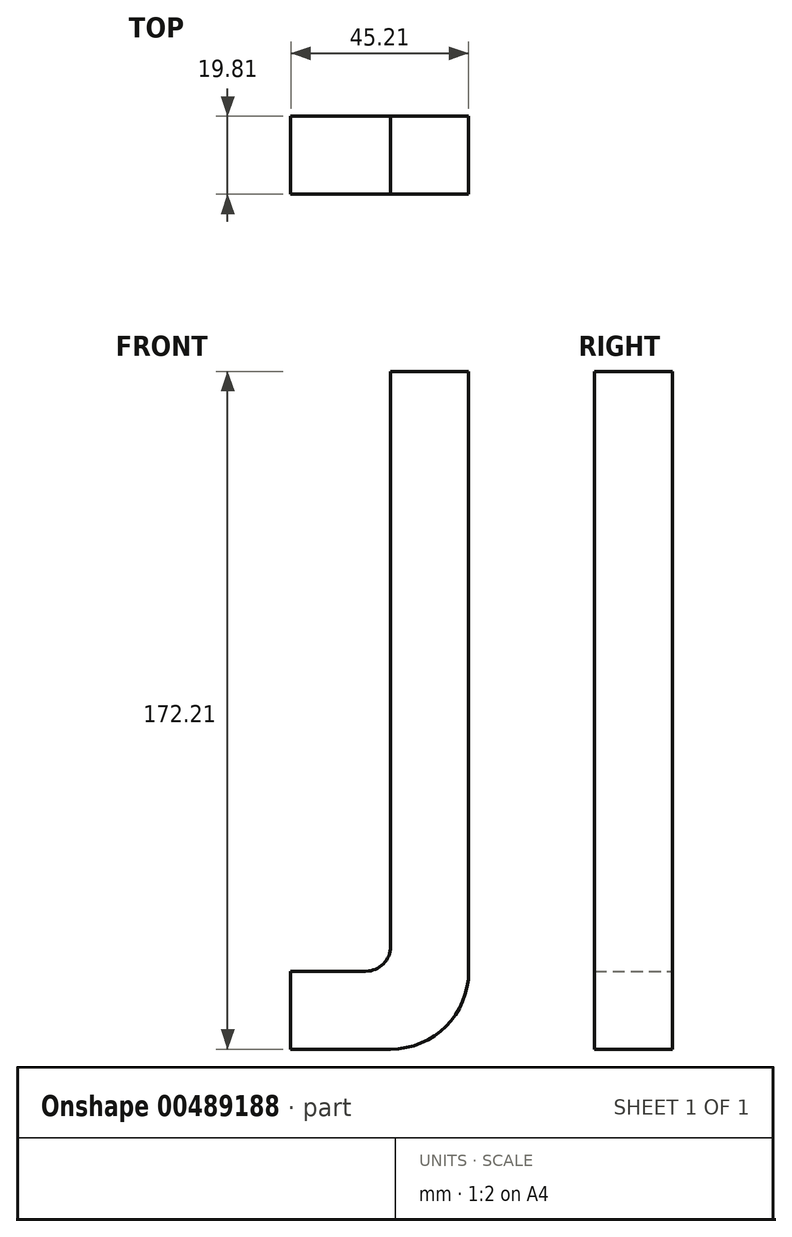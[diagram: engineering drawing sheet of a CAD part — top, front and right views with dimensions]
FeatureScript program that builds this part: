
annotation { "Feature Type Name" : "Feature", "Feature Type Description" : "" }
export const myFeature = defineFeature(function(context is Context, id is Id, definition is map)
    precondition{}
    {
        {
            var Q0;
            Q0=qCreatedBy(makeId("Front.planeOp"),FACE);
            var sketch = newSketch(context, id + "F0", { "sketchPlane" : qUnion([Q0])});
            skLineSegment(sketch, "E0.bottom", {"start": v(-36.32, 115.57) * mm, "end": v(-16.51, 115.57) * mm});
            skLineSegment(sketch, "E0.left", {"start": v(-36.32, 115.57) * mm, "end": v(-36.32, -30.48) * mm});
            skLineSegment(sketch, "E0.right", {"start": v(-16.51, 115.57) * mm, "end": v(-16.51, -36.83) * mm});
            skArc(sketch, "E1", {"start": v(-36.32, -56.64) * mm, "mid": v(-22.32, -50.84) * mm, "end": v(-16.51, -36.83) * mm});
            skLineSegment(sketch, "E2.bottom", {"start": v(-36.32, -56.64) * mm, "end": v(-61.72, -56.64) * mm});
            skLineSegment(sketch, "E2.top", {"start": v(-42.67, -36.83) * mm, "end": v(-61.72, -36.83) * mm});
            skLineSegment(sketch, "E2.right", {"start": v(-61.72, -56.64) * mm, "end": v(-61.72, -36.83) * mm});
            skArc(sketch, "E3.filletArc", {"start": v(-42.67, -36.83) * mm, "mid": v(-38.18, -34.97) * mm, "end": v(-36.32, -30.48) * mm});
            skLineSegment(sketch, "E4", {"start": v(-16.51, -36.83) * mm, "end": v(-36.32, -36.83) * mm, "construction": true});
            skLineSegment(sketch, "E5", {"start": v(-36.32, -36.83) * mm, "end": v(-36.32, -56.64) * mm, "construction": true});
            skSolve(sketch);
        }
        {
            var Q0;
            Q0 = qSketchRegion(id + "F0", true);
            extrude(context, id + "F1", {"entities" : qUnion([Q0]), "depth" : 19.8 * mm, "offsetDistance" : 25.4 * mm});
        }
    });
